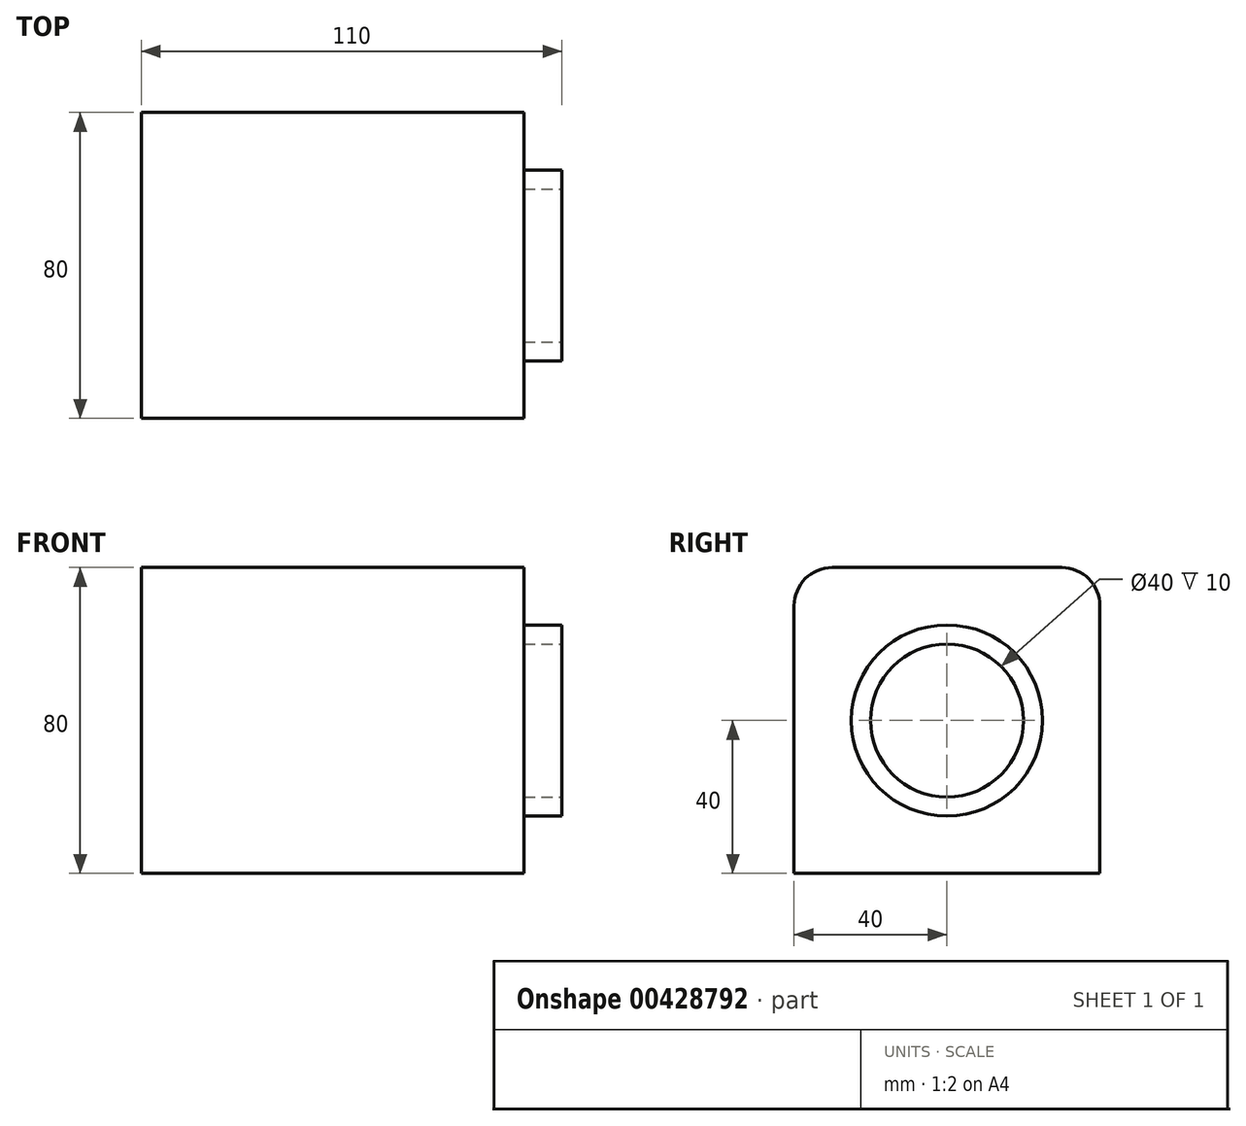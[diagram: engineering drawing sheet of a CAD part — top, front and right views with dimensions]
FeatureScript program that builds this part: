
annotation { "Feature Type Name" : "Feature", "Feature Type Description" : "" }
export const myFeature = defineFeature(function(context is Context, id is Id, definition is map)
    precondition{}
    {
        {
            var Q0;
            Q0=qCreatedBy(makeId("Top.planeOp"),FACE);
            var sketch = newSketch(context, id + "F0", { "sketchPlane" : qUnion([Q0])});
            skLineSegment(sketch, "E0.bottom", {"start": v(50, 40) * mm, "end": v(-50, 40) * mm});
            skLineSegment(sketch, "E0.top", {"start": v(50, -40) * mm, "end": v(-50, -40) * mm});
            skLineSegment(sketch, "E0.left", {"start": v(50, 40) * mm, "end": v(50, -40) * mm});
            skLineSegment(sketch, "E0.right", {"start": v(-50, 40) * mm, "end": v(-50, -40) * mm});
            skPoint(sketch, "E0.middle", {"position": v(0, 0) * mm});
            skSolve(sketch);
        }
        {
            var Q0;
            Q0=qSketchRegion(id+"F0",true);
            extrude(context, id + "F1", {"entities" : qUnion([Q0]), "depth" : 80 * mm});
        }
        {
            var Q0;
            Q0=makeQuery(id+"F1.opExtrude","CAP_EDGE",EDGE,{"disambiguationData":[OSD([sQuery(id+"F0.wireOp",EDGE,"E0.top")])],"isStart":false});
            var Q1;
            Q1=makeQuery(id+"F1.opExtrude","CAP_EDGE",EDGE,{"disambiguationData":[OSD([sQuery(id+"F0.wireOp",EDGE,"E0.bottom")])],"isStart":false});
            fillet(context, id + "F2", {"entities" : qUnion([Q0, Q1]), "radius" : 10 * mm, "tangentPropagation" : true, "allowEdgeOverflow" : false});
        }
        {
            var Q0;
            Q0=makeQuery(id+"F1.opExtrude","SWEPT_FACE",FACE,{"disambiguationData":[OSD([sQuery(id+"F0.wireOp",EDGE,"E0.left")])]});
            var sketch = newSketch(context, id + "F3", { "sketchPlane" : qUnion([Q0])});
            skLineSegment(sketch, "E1", {"start": v(0, 80) * mm, "end": v(0, 0) * mm, "construction": true});
            skLineSegment(sketch, "E2", {"start": v(0, 40) * mm, "end": v(-40, 40) * mm, "construction": true});
            skCircle(sketch, "E3", {"center": v(0, 40) * mm, "radius": 25 * mm});
            skSolve(sketch);
        }
        {
            var Q0;
            Q0=qSketchRegion(id+"F3",true);
            extrude(context, id + "F4", {"entities" : qUnion([Q0]), "operationType" : NewBodyOperationType.ADD, "depth" : 10 * mm});
        }
        {
            var Q0;
            Q0=makeQuery(id+"F4.opExtrude","CAP_FACE",FACE,{"disambiguationData":[OSD([sQuery(id+"F3.wireOp",EDGE,"E3")])],"isStart":false});
            var sketch = newSketch(context, id + "F5", { "sketchPlane" : qUnion([Q0])});
            skCircle(sketch, "E4", {"center": v(0, 40) * mm, "radius": 20 * mm});
            skSolve(sketch);
        }
        {
            var Q0;
            Q0=makeQuery(id+"F5.imprint","IMPRINT",FACE,{"disambiguationData":[TD([[makeQuery(id+"F5.imprint","IMPRINT",EDGE,{"derivedFrom":sQuery(id+"F5.wireOp",EDGE,"E4")}),1.0]])]});
            var Q1;
            Q1=sQuery(id+"F5.wireOp",EDGE,"E4");
            extrude(context, id + "F6", {"entities" : qUnion([Q0]), "operationType" : NewBodyOperationType.REMOVE, "surfaceEntities" : qUnion([Q1]), "oppositeDirection" : true, "depth" : 10 * mm});
        }
    });
